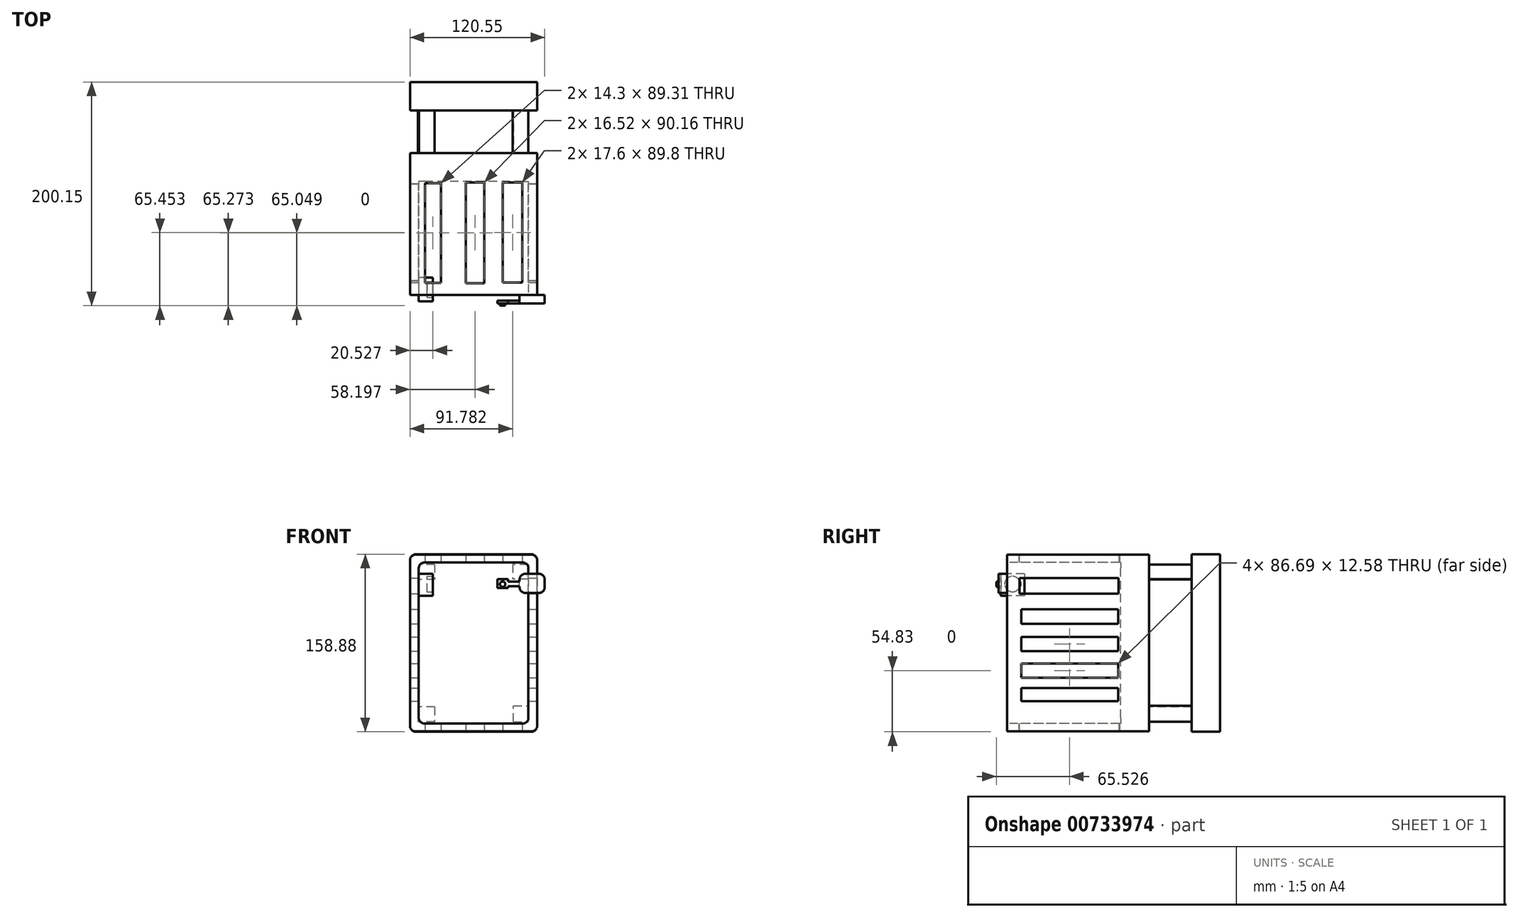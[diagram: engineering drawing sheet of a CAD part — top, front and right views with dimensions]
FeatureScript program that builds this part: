
annotation { "Feature Type Name" : "Feature", "Feature Type Description" : "" }
export const myFeature = defineFeature(function(context is Context, id is Id, definition is map)
    precondition{}
    {
        {
            var Q0;
            Q0=qCreatedBy(makeId("Front.planeOp"),FACE);
            var sketch = newSketch(context, id + "F0", { "sketchPlane" : qUnion([Q0])});
            skLineSegment(sketch, "E0.bottom", {"start": v(56.94, -79.1) * mm, "end": v(-56.94, -79.1) * mm});
            skLineSegment(sketch, "E0.top", {"start": v(56.94, 79.1) * mm, "end": v(-56.94, 79.1) * mm});
            skLineSegment(sketch, "E0.left", {"start": v(56.94, -79.1) * mm, "end": v(56.94, 79.1) * mm});
            skLineSegment(sketch, "E0.right", {"start": v(-56.94, -79.1) * mm, "end": v(-56.94, 79.1) * mm});
            skPoint(sketch, "E0.middle", {"position": v(0, 0) * mm});
            skSolve(sketch);
        }
        {
            var Q0;
            Q0=makeQuery(id+"F0.imprint","IMPRINT",FACE,{"disambiguationData":[TD([[makeQuery(id+"F0.imprint","IMPRINT",EDGE,{"derivedFrom":sQuery(id+"F0.wireOp",EDGE,"E0.bottom")}),-1.0]])]});
            extrude(context, id + "F1", {"entities" : qUnion([Q0]), "depth" : 127 * mm, "offsetDistance" : 25.4 * mm});
        }
        {
            var Q0;
            Q0=makeQuery(id+"F1.opExtrude","CAP_FACE",FACE,{"disambiguationData":[OSD([sQuery(id+"F0.wireOp",EDGE,"E0.bottom"),sQuery(id+"F0.wireOp",EDGE,"E0.top"),sQuery(id+"F0.wireOp",EDGE,"E0.left"),sQuery(id+"F0.wireOp",EDGE,"E0.right")])],"isStart":false});
            var sketch = newSketch(context, id + "F2", { "sketchPlane" : qUnion([Q0])});
            skLineSegment(sketch, "E1.bottom", {"start": v(49.08, -72.01) * mm, "end": v(-49.08, -72.01) * mm});
            skLineSegment(sketch, "E1.top", {"start": v(49.08, 72.01) * mm, "end": v(-49.08, 72.01) * mm});
            skLineSegment(sketch, "E1.left", {"start": v(49.08, -72.01) * mm, "end": v(49.08, 72.01) * mm});
            skLineSegment(sketch, "E1.right", {"start": v(-49.08, -72.01) * mm, "end": v(-49.08, 72.01) * mm});
            skPoint(sketch, "E1.middle", {"position": v(0, 0) * mm});
            skSolve(sketch);
        }
        {
            var Q0;
            Q0=makeQuery(id+"F2.imprint","IMPRINT",FACE,{"disambiguationData":[TD([[makeQuery(id+"F2.imprint","IMPRINT",EDGE,{"derivedFrom":sQuery(id+"F2.wireOp",EDGE,"E1.bottom")}),-1.0]])]});
            extrude(context, id + "F3", {"entities" : qUnion([Q0]), "operationType" : NewBodyOperationType.REMOVE, "oppositeDirection" : true, "depth" : 101.6 * mm, "offsetDistance" : 25.4 * mm});
        }
        {
            var Q0;
            Q0=makeQuery(id+"F1.opExtrude","SWEPT_FACE",FACE,{"disambiguationData":[OSD([sQuery(id+"F0.wireOp",EDGE,"E0.bottom")])]});
            var sketch = newSketch(context, id + "F4", { "sketchPlane" : qUnion([Q0])});
            skLineSegment(sketch, "E2.bottom", {"start": v(-43.56, 116.26) * mm, "end": v(-29.26, 116.26) * mm});
            skLineSegment(sketch, "E2.top", {"start": v(-43.56, 26.95) * mm, "end": v(-29.26, 26.95) * mm});
            skLineSegment(sketch, "E2.left", {"start": v(-43.56, 116.26) * mm, "end": v(-43.56, 26.95) * mm});
            skLineSegment(sketch, "E2.right", {"start": v(-29.26, 116.26) * mm, "end": v(-29.26, 26.95) * mm});
            skSolve(sketch);
        }
        {
            var Q0;
            Q0 = qSketchRegion(id + "F4", true);
            extrude(context, id + "F5", {"entities" : qUnion([Q0]), "operationType" : NewBodyOperationType.REMOVE, "endBound" : BoundingType.THROUGH_ALL, "oppositeDirection" : true, "depth" : 25.4 * mm, "offsetDistance" : 25.4 * mm});
        }
        {
            var Q0;
            Q0=makeQuery(id+"F1.opExtrude","SWEPT_FACE",FACE,{"disambiguationData":[OSD([sQuery(id+"F0.wireOp",EDGE,"E0.bottom")])]});
            var sketch = newSketch(context, id + "F6", { "sketchPlane" : qUnion([Q0])});
            skLineSegment(sketch, "E3.bottom", {"start": v(-7, 116.46) * mm, "end": v(9.52, 116.46) * mm});
            skLineSegment(sketch, "E3.top", {"start": v(-7, 26.3) * mm, "end": v(9.52, 26.3) * mm});
            skLineSegment(sketch, "E3.left", {"start": v(-7, 116.46) * mm, "end": v(-7, 26.3) * mm});
            skLineSegment(sketch, "E3.right", {"start": v(9.52, 116.46) * mm, "end": v(9.52, 26.3) * mm});
            skSolve(sketch);
        }
        {
            var Q0;
            Q0 = qSketchRegion(id + "F6", true);
            extrude(context, id + "F7", {"entities" : qUnion([Q0]), "operationType" : NewBodyOperationType.REMOVE, "endBound" : BoundingType.THROUGH_ALL, "oppositeDirection" : true, "depth" : 25.4 * mm, "offsetDistance" : 25.4 * mm});
        }
        {
            var Q0;
            Q0=makeQuery(id+"F1.opExtrude","SWEPT_FACE",FACE,{"disambiguationData":[OSD([sQuery(id+"F0.wireOp",EDGE,"E0.bottom")])]});
            var sketch = newSketch(context, id + "F8", { "sketchPlane" : qUnion([Q0])});
            skLineSegment(sketch, "E4.bottom", {"start": v(26.04, 116.1) * mm, "end": v(43.64, 116.1) * mm});
            skLineSegment(sketch, "E4.top", {"start": v(26.04, 26.3) * mm, "end": v(43.64, 26.3) * mm});
            skLineSegment(sketch, "E4.left", {"start": v(26.04, 116.1) * mm, "end": v(26.04, 26.3) * mm});
            skLineSegment(sketch, "E4.right", {"start": v(43.64, 116.1) * mm, "end": v(43.64, 26.3) * mm});
            skSolve(sketch);
        }
        {
            var Q0;
            Q0 = qSketchRegion(id + "F8", true);
            extrude(context, id + "F9", {"entities" : qUnion([Q0]), "operationType" : NewBodyOperationType.REMOVE, "endBound" : BoundingType.THROUGH_ALL, "oppositeDirection" : true, "depth" : 25.4 * mm, "offsetDistance" : 25.4 * mm});
        }
        {
            var Q0;
            Q0=makeQuery(id+"F1.opExtrude","SWEPT_FACE",FACE,{"disambiguationData":[OSD([sQuery(id+"F0.wireOp",EDGE,"E0.left")])]});
            var sketch = newSketch(context, id + "F10", { "sketchPlane" : qUnion([Q0])});
            skLineSegment(sketch, "E5.bottom", {"start": v(-115.88, 58.3) * mm, "end": v(-27.27, 58.3) * mm});
            skLineSegment(sketch, "E5.top", {"start": v(-115.88, 44.33) * mm, "end": v(-27.27, 44.33) * mm});
            skLineSegment(sketch, "E5.left", {"start": v(-115.88, 58.3) * mm, "end": v(-115.88, 44.33) * mm});
            skLineSegment(sketch, "E5.right", {"start": v(-27.27, 58.3) * mm, "end": v(-27.27, 44.33) * mm});
            skSolve(sketch);
        }
        {
            var Q0;
            Q0=makeQuery(id+"F10.imprint","IMPRINT",FACE,{"disambiguationData":[TD([[makeQuery(id+"F10.imprint","IMPRINT",EDGE,{"derivedFrom":sQuery(id+"F10.wireOp",EDGE,"E5.bottom")}),-1.0]])]});
            extrude(context, id + "F11", {"entities" : qUnion([Q0]), "operationType" : NewBodyOperationType.REMOVE, "endBound" : BoundingType.THROUGH_ALL, "oppositeDirection" : true, "depth" : 25.4 * mm, "offsetDistance" : 25.4 * mm});
        }
        {
            var Q0;
            Q0=makeQuery(id+"F1.opExtrude","SWEPT_FACE",FACE,{"disambiguationData":[OSD([sQuery(id+"F0.wireOp",EDGE,"E0.left")])]});
            var sketch = newSketch(context, id + "F12", { "sketchPlane" : qUnion([Q0])});
            skLineSegment(sketch, "E6.bottom", {"start": v(-114.2, 30.06) * mm, "end": v(-27.78, 30.06) * mm});
            skLineSegment(sketch, "E6.top", {"start": v(-114.2, 17.2) * mm, "end": v(-27.78, 17.2) * mm});
            skLineSegment(sketch, "E6.left", {"start": v(-114.2, 30.06) * mm, "end": v(-114.2, 17.2) * mm});
            skLineSegment(sketch, "E6.right", {"start": v(-27.78, 30.06) * mm, "end": v(-27.78, 17.2) * mm});
            skPoint(sketch, "E7.oppositeSnap0", {"position": v(-27.78, 23.63) * mm});
            skLineSegment(sketch, "E7.bottom", {"start": v(-114.47, 5.45) * mm, "end": v(-27.78, 5.45) * mm});
            skLineSegment(sketch, "E7.top", {"start": v(-114.47, -7.13) * mm, "end": v(-27.78, -7.13) * mm});
            skLineSegment(sketch, "E7.left", {"start": v(-114.47, 5.45) * mm, "end": v(-114.47, -7.13) * mm});
            skLineSegment(sketch, "E7.right", {"start": v(-27.78, 5.45) * mm, "end": v(-27.78, -7.13) * mm});
            skLineSegment(sketch, "E8.bottom", {"start": v(-114.47, -18.32) * mm, "end": v(-27.78, -18.32) * mm});
            skLineSegment(sketch, "E8.top", {"start": v(-114.47, -30.9) * mm, "end": v(-27.78, -30.9) * mm});
            skLineSegment(sketch, "E8.left", {"start": v(-114.47, -18.32) * mm, "end": v(-114.47, -30.9) * mm});
            skLineSegment(sketch, "E8.right", {"start": v(-27.78, -18.32) * mm, "end": v(-27.78, -30.9) * mm});
            skLineSegment(sketch, "E9.bottom", {"start": v(-114.47, -40.13) * mm, "end": v(-27.78, -40.13) * mm});
            skLineSegment(sketch, "E9.top", {"start": v(-114.47, -52.16) * mm, "end": v(-27.78, -52.16) * mm});
            skLineSegment(sketch, "E9.left", {"start": v(-114.47, -40.13) * mm, "end": v(-114.47, -52.16) * mm});
            skLineSegment(sketch, "E9.right", {"start": v(-27.78, -40.13) * mm, "end": v(-27.78, -52.16) * mm});
            skSolve(sketch);
        }
        {
            var Q0;
            Q0 = qSketchRegion(id + "F12", true);
            extrude(context, id + "F13", {"entities" : qUnion([Q0]), "operationType" : NewBodyOperationType.REMOVE, "endBound" : BoundingType.THROUGH_ALL, "oppositeDirection" : true, "depth" : 25.4 * mm, "offsetDistance" : 25.4 * mm});
        }
        {
            var Q0;
            Q0=makeQuery(id+"F1.opExtrude","SWEPT_EDGE",EDGE,{"disambiguationData":[OSD([sQuery(id+"F0.wireOp",EDGE,"E0.bottom"),sQuery(id+"F0.wireOp",EDGE,"E0.left")])]});
            var Q1;
            Q1=makeQuery(id+"F1.opExtrude","SWEPT_EDGE",EDGE,{"disambiguationData":[OSD([sQuery(id+"F0.wireOp",EDGE,"E0.bottom"),sQuery(id+"F0.wireOp",EDGE,"E0.right")])]});
            var Q2;
            Q2=makeQuery(id+"F1.opExtrude","SWEPT_EDGE",EDGE,{"disambiguationData":[OSD([sQuery(id+"F0.wireOp",EDGE,"E0.top"),sQuery(id+"F0.wireOp",EDGE,"E0.left")])]});
            var Q3;
            Q3=makeQuery(id+"F1.opExtrude","SWEPT_EDGE",EDGE,{"disambiguationData":[OSD([sQuery(id+"F0.wireOp",EDGE,"E0.top"),sQuery(id+"F0.wireOp",EDGE,"E0.right")])]});
            var Q4;
            Q4=makeQuery(id+"F3.boolean.opBoolean","COPY",EDGE,{"derivedFrom":makeQuery(id+"F3.opExtrude","SWEPT_EDGE",EDGE,{"disambiguationData":[OSD([sQuery(id+"F2.wireOp",EDGE,"E1.top"),sQuery(id+"F2.wireOp",EDGE,"E1.left")])]})});
            var Q5;
            Q5=makeQuery(id+"F3.boolean.opBoolean","COPY",EDGE,{"derivedFrom":makeQuery(id+"F3.opExtrude","SWEPT_EDGE",EDGE,{"disambiguationData":[OSD([sQuery(id+"F2.wireOp",EDGE,"E1.bottom"),sQuery(id+"F2.wireOp",EDGE,"E1.left")])]})});
            var Q6;
            Q6=makeQuery(id+"F3.boolean.opBoolean","COPY",EDGE,{"derivedFrom":makeQuery(id+"F3.opExtrude","SWEPT_EDGE",EDGE,{"disambiguationData":[OSD([sQuery(id+"F2.wireOp",EDGE,"E1.bottom"),sQuery(id+"F2.wireOp",EDGE,"E1.right")])]})});
            var Q7;
            Q7=makeQuery(id+"F3.boolean.opBoolean","COPY",EDGE,{"derivedFrom":makeQuery(id+"F3.opExtrude","SWEPT_EDGE",EDGE,{"disambiguationData":[OSD([sQuery(id+"F2.wireOp",EDGE,"E1.top"),sQuery(id+"F2.wireOp",EDGE,"E1.right")])]})});
            fillet(context, id + "F14", {"entities" : qUnion([Q0, Q1, Q2, Q3, Q4, Q5, Q6, Q7]), "radius" : 5.08 * mm, "tangentPropagation" : true, "allowEdgeOverflow" : false});
        }
        {
            var Q0;
            Q0=makeQuery(id+"F1.opExtrude","CAP_FACE",FACE,{"disambiguationData":[OSD([sQuery(id+"F0.wireOp",EDGE,"E0.bottom"),sQuery(id+"F0.wireOp",EDGE,"E0.top"),sQuery(id+"F0.wireOp",EDGE,"E0.left"),sQuery(id+"F0.wireOp",EDGE,"E0.right")])],"isStart":true});
            var sketch = newSketch(context, id + "F15", { "sketchPlane" : qUnion([Q0])});
            skLineSegment(sketch, "E10.bottom", {"start": v(-48.8, 70.33) * mm, "end": v(-34.82, 70.33) * mm});
            skLineSegment(sketch, "E10.top", {"start": v(-48.8, 57.2) * mm, "end": v(-34.82, 57.2) * mm});
            skLineSegment(sketch, "E10.left", {"start": v(-48.8, 70.33) * mm, "end": v(-48.8, 57.2) * mm});
            skLineSegment(sketch, "E10.right", {"start": v(-34.82, 70.33) * mm, "end": v(-34.82, 57.2) * mm});
            skLineSegment(sketch, "E11.bottom", {"start": v(34.82, 70.33) * mm, "end": v(48.8, 70.33) * mm});
            skLineSegment(sketch, "E11.top", {"start": v(34.82, 56.91) * mm, "end": v(48.8, 56.91) * mm});
            skLineSegment(sketch, "E11.left", {"start": v(34.82, 70.33) * mm, "end": v(34.82, 56.91) * mm});
            skLineSegment(sketch, "E11.right", {"start": v(48.8, 70.33) * mm, "end": v(48.8, 56.91) * mm});
            skLineSegment(sketch, "E12.bottom", {"start": v(34.82, -57.2) * mm, "end": v(49.92, -57.2) * mm});
            skLineSegment(sketch, "E12.top", {"start": v(34.82, -70.33) * mm, "end": v(49.92, -70.33) * mm});
            skLineSegment(sketch, "E12.left", {"start": v(34.82, -57.2) * mm, "end": v(34.82, -70.33) * mm});
            skLineSegment(sketch, "E12.right", {"start": v(49.92, -57.2) * mm, "end": v(49.92, -70.33) * mm});
            skLineSegment(sketch, "E13.bottom", {"start": v(-35.66, -70.33) * mm, "end": v(-49.08, -70.33) * mm});
            skLineSegment(sketch, "E13.top", {"start": v(-35.66, -56.07) * mm, "end": v(-49.08, -56.07) * mm});
            skLineSegment(sketch, "E13.left", {"start": v(-35.66, -70.33) * mm, "end": v(-35.66, -56.07) * mm});
            skLineSegment(sketch, "E13.right", {"start": v(-49.08, -70.33) * mm, "end": v(-49.08, -56.07) * mm});
            skSolve(sketch);
        }
        {
            var Q0;
            Q0 = qSketchRegion(id + "F15", true);
            extrude(context, id + "F16", {"entities" : qUnion([Q0]), "operationType" : NewBodyOperationType.ADD, "depth" : 38.1 * mm, "offsetDistance" : 25.4 * mm});
        }
        {
            var Q0;
            Q0=makeQuery(id+"F16.opExtrude","CAP_FACE",FACE,{"disambiguationData":[OSD([sQuery(id+"F15.wireOp",EDGE,"E12.bottom"),sQuery(id+"F15.wireOp",EDGE,"E12.top"),sQuery(id+"F15.wireOp",EDGE,"E12.left"),sQuery(id+"F15.wireOp",EDGE,"E12.right")])],"isStart":false});
            var sketch = newSketch(context, id + "F17", { "sketchPlane" : qUnion([Q0])});
            skLineSegment(sketch, "E14.bottom", {"start": v(56.72, -79.44) * mm, "end": v(-56.72, -79.44) * mm});
            skLineSegment(sketch, "E14.top", {"start": v(56.72, 79.44) * mm, "end": v(-56.72, 79.44) * mm});
            skLineSegment(sketch, "E14.left", {"start": v(56.72, -79.44) * mm, "end": v(56.72, 79.44) * mm});
            skLineSegment(sketch, "E14.right", {"start": v(-56.72, -79.44) * mm, "end": v(-56.72, 79.44) * mm});
            skPoint(sketch, "E14.middle", {"position": v(0, 0) * mm});
            skSolve(sketch);
        }
        {
            var Q0;
            Q0 = qSketchRegion(id + "F17", true);
            extrude(context, id + "F18", {"entities" : qUnion([Q0]), "operationType" : NewBodyOperationType.ADD, "depth" : 25.4 * mm, "offsetDistance" : 25.4 * mm});
        }
        {
            var Q0;
            Q0=makeQuery(id+"F18.opExtrude","SWEPT_EDGE",EDGE,{"disambiguationData":[OSD([sQuery(id+"F17.wireOp",EDGE,"E14.bottom"),sQuery(id+"F17.wireOp",EDGE,"E14.left")])]});
            var Q1;
            Q1=makeQuery(id+"F18.opExtrude","SWEPT_EDGE",EDGE,{"disambiguationData":[OSD([sQuery(id+"F17.wireOp",EDGE,"E14.bottom"),sQuery(id+"F17.wireOp",EDGE,"E14.right")])]});
            var Q2;
            Q2=makeQuery(id+"F18.opExtrude","SWEPT_EDGE",EDGE,{"disambiguationData":[OSD([sQuery(id+"F17.wireOp",EDGE,"E14.top"),sQuery(id+"F17.wireOp",EDGE,"E14.right")])]});
            var Q3;
            Q3=makeQuery(id+"F18.opExtrude","SWEPT_EDGE",EDGE,{"disambiguationData":[OSD([sQuery(id+"F17.wireOp",EDGE,"E14.top"),sQuery(id+"F17.wireOp",EDGE,"E14.left")])]});
            fillet(context, id + "F19", {"entities" : qUnion([Q0, Q1, Q2, Q3]), "radius" : 5.08 * mm, "tangentPropagation" : true, "allowEdgeOverflow" : false});
        }
        {
            var Q0;
            Q0=makeQuery(id+"F1.opExtrude","CAP_FACE",FACE,{"disambiguationData":[OSD([sQuery(id+"F0.wireOp",EDGE,"E0.bottom"),sQuery(id+"F0.wireOp",EDGE,"E0.top"),sQuery(id+"F0.wireOp",EDGE,"E0.left"),sQuery(id+"F0.wireOp",EDGE,"E0.right")])],"isStart":false});
            var sketch = newSketch(context, id + "F20", { "sketchPlane" : qUnion([Q0])});
            skLineSegment(sketch, "E15.bottom", {"start": v(63.61, 44.8) * mm, "end": v(41.14, 44.8) * mm});
            skLineSegment(sketch, "E15.top", {"start": v(63.61, 61.93) * mm, "end": v(41.14, 61.93) * mm});
            skLineSegment(sketch, "E15.left", {"start": v(63.61, 44.8) * mm, "end": v(63.61, 61.93) * mm});
            skLineSegment(sketch, "E15.right", {"start": v(41.14, 44.8) * mm, "end": v(41.14, 61.93) * mm});
            skPoint(sketch, "E15.middle", {"position": v(52.38, 53.36) * mm});
            skSolve(sketch);
        }
        {
            var Q0;
            Q0 = qSketchRegion(id + "F20", true);
            extrude(context, id + "F21", {"entities" : qUnion([Q0]), "operationType" : NewBodyOperationType.ADD, "depth" : 7.62 * mm, "offsetDistance" : 25.4 * mm});
        }
        {
            var Q0;
            Q0=makeQuery(id+"F21.opExtrude","SWEPT_EDGE",EDGE,{"disambiguationData":[OSD([sQuery(id+"F20.wireOp",EDGE,"E15.top"),sQuery(id+"F20.wireOp",EDGE,"E15.left")])]});
            var Q1;
            Q1=makeQuery(id+"F21.opExtrude","SWEPT_EDGE",EDGE,{"disambiguationData":[OSD([sQuery(id+"F20.wireOp",EDGE,"E15.bottom"),sQuery(id+"F20.wireOp",EDGE,"E15.left")])]});
            var Q2;
            Q2=makeQuery(id+"F21.opExtrude","SWEPT_EDGE",EDGE,{"disambiguationData":[OSD([sQuery(id+"F20.wireOp",EDGE,"E15.top"),sQuery(id+"F20.wireOp",EDGE,"E15.right")])]});
            var Q3;
            Q3=makeQuery(id+"F21.opExtrude","SWEPT_EDGE",EDGE,{"disambiguationData":[OSD([sQuery(id+"F20.wireOp",EDGE,"E15.bottom"),sQuery(id+"F20.wireOp",EDGE,"E15.right")])]});
            fillet(context, id + "F22", {"entities" : qUnion([Q0, Q1, Q2, Q3]), "radius" : 5.08 * mm, "tangentPropagation" : true, "allowEdgeOverflow" : false});
        }
        {
            var Q0;
            Q0=makeQuery(id+"F21.opExtrude","CAP_FACE",FACE,{"disambiguationData":[OSD([sQuery(id+"F20.wireOp",EDGE,"E15.bottom"),sQuery(id+"F20.wireOp",EDGE,"E15.top"),sQuery(id+"F20.wireOp",EDGE,"E15.left"),sQuery(id+"F20.wireOp",EDGE,"E15.right")])],"isStart":false});
            var sketch = newSketch(context, id + "F23", { "sketchPlane" : qUnion([Q0])});
            skLineSegment(sketch, "E16.bottom", {"start": v(29.34, 54.94) * mm, "end": v(47.82, 54.94) * mm});
            skLineSegment(sketch, "E16.top", {"start": v(29.34, 51) * mm, "end": v(47.82, 51) * mm});
            skLineSegment(sketch, "E16.left", {"start": v(29.34, 54.94) * mm, "end": v(29.34, 51) * mm});
            skLineSegment(sketch, "E16.right", {"start": v(47.82, 54.94) * mm, "end": v(47.82, 51) * mm});
            skLineSegment(sketch, "E17.bottom", {"start": v(21.3, 49.28) * mm, "end": v(30.72, 49.28) * mm});
            skLineSegment(sketch, "E17.top", {"start": v(21.3, 57.07) * mm, "end": v(30.72, 57.07) * mm});
            skLineSegment(sketch, "E17.left", {"start": v(21.3, 49.28) * mm, "end": v(21.3, 57.07) * mm});
            skLineSegment(sketch, "E17.right", {"start": v(30.72, 49.28) * mm, "end": v(30.72, 57.07) * mm});
            skCircle(sketch, "E18", {"center": v(25.4, 52.57) * mm, "radius": 1.89 * mm});
            skSolve(sketch);
        }
        {
            var Q0;
            Q0=makeQuery(id+"F23.imprint","IMPRINT",FACE,{"disambiguationData":[TD([[makeQuery(id+"F23.imprint","IMPRINT",EDGE,{"derivedFrom":sQuery(id+"F23.wireOp",EDGE,"E18")}),1.0]])]});
            var Q1;
            {var subQ0=sQuery(id+"F23.wireOp",EDGE,"E16.left");Q1=makeQuery(id+"F23.imprint","IMPRINT",FACE,{"disambiguationData":[TD([[makeQuery(id+"F23.imprint","IMPRINT",EDGE,{"derivedFrom":subQ0}),-1.0]])]});}
            var Q2;
            {var subQ0=sQuery(id+"F23.wireOp",EDGE,"E16.left");Q2=makeQuery(id+"F23.imprint","IMPRINT",FACE,{"disambiguationData":[TD([[makeQuery(id+"F23.imprint","IMPRINT",EDGE,{"derivedFrom":subQ0}),1.0]])]});}
            var Q3;
            {var subQ0=sQuery(id+"F23.wireOp",EDGE,"E17.right");var subQ1=sQuery(id+"F23.wireOp",EDGE,"E16.bottom");var subQ2=makeQuery(id+"F23.imprint","INTERSECT",VERTEX,{"derivedFrom":[subQ1,subQ0]});Q3=makeQuery(id+"F23.imprint","IMPRINT",FACE,{"disambiguationData":[TD([[makeQuery(id+"F23.imprint","IMPRINT",EDGE,{"disambiguationData":[TD([[subQ2,-1.0]])],"derivedFrom":subQ1}),-1.0]])]});}
            extrude(context, id + "F24", {"entities" : qUnion([Q0, Q1, Q2, Q3]), "operationType" : NewBodyOperationType.ADD, "oppositeDirection" : true, "depth" : 2.54 * mm, "offsetDistance" : 25.4 * mm});
        }
        {
            var Q0;
            {var subQ0=sQuery(id+"F20.wireOp",EDGE,"E15.right");Q0=makeQuery(id+"F24.boolean.opBoolean","MERGE",FACE,{"derivedFrom":[makeQuery(id+"F21.opExtrude","CAP_FACE",FACE,{"disambiguationData":[OSD([sQuery(id+"F20.wireOp",EDGE,"E15.bottom"),sQuery(id+"F20.wireOp",EDGE,"E15.top"),sQuery(id+"F20.wireOp",EDGE,"E15.left"),subQ0])],"isStart":false}),makeQuery(id+"F24.opExtrude","CAP_FACE",FACE,{"disambiguationData":[OSD([subQ0,sQuery(id+"F23.wireOp",EDGE,"E16.bottom"),sQuery(id+"F23.wireOp",EDGE,"E16.top"),sQuery(id+"F23.wireOp",EDGE,"E17.bottom"),sQuery(id+"F23.wireOp",EDGE,"E17.top"),sQuery(id+"F23.wireOp",EDGE,"E17.left"),sQuery(id+"F23.wireOp",EDGE,"E17.right")])],"isStart":true})]});}
            var sketch = newSketch(context, id + "F25", { "sketchPlane" : qUnion([Q0])});
            skCircle(sketch, "E19", {"center": v(26, 52.71) * mm, "radius": 2.4 * mm});
            skPoint(sketch, "E19.centerSnap0", {"position": v(26, 57.07) * mm});
            skSolve(sketch);
        }
        {
            var Q0;
            Q0 = qSketchRegion(id + "F25", true);
            extrude(context, id + "F26", {"entities" : qUnion([Q0]), "operationType" : NewBodyOperationType.ADD, "depth" : 2.03 * mm, "offsetDistance" : 25.4 * mm});
        }
        {
            var Q0;
            Q0=makeQuery(id+"F3.boolean.opBoolean","COPY",FACE,{"derivedFrom":makeQuery(id+"F3.opExtrude","SWEPT_FACE",FACE,{"disambiguationData":[OSD([sQuery(id+"F2.wireOp",EDGE,"E1.right")])]})});
            var sketch = newSketch(context, id + "F27", { "sketchPlane" : qUnion([Q0])});
            skLineSegment(sketch, "E20.bottom", {"start": v(-111.52, 62.03) * mm, "end": v(-132.82, 62.03) * mm});
            skLineSegment(sketch, "E20.top", {"start": v(-111.52, 42.24) * mm, "end": v(-132.82, 42.24) * mm});
            skLineSegment(sketch, "E20.left", {"start": v(-111.52, 62.03) * mm, "end": v(-111.52, 42.24) * mm});
            skLineSegment(sketch, "E20.right", {"start": v(-132.82, 62.03) * mm, "end": v(-132.82, 42.24) * mm});
            skSolve(sketch);
        }
        {
            var Q0;
            Q0 = qSketchRegion(id + "F27", true);
            extrude(context, id + "F28", {"entities" : qUnion([Q0]), "operationType" : NewBodyOperationType.ADD, "depth" : 12.7 * mm, "offsetDistance" : 25.4 * mm});
        }
        {
            var Q0;
            Q0=makeQuery(id+"F28.opExtrude","CAP_FACE",FACE,{"disambiguationData":[OSD([sQuery(id+"F27.wireOp",EDGE,"E20.bottom"),sQuery(id+"F27.wireOp",EDGE,"E20.top"),sQuery(id+"F27.wireOp",EDGE,"E20.left"),sQuery(id+"F27.wireOp",EDGE,"E20.right")])],"isStart":false});
            var sketch = newSketch(context, id + "F29", { "sketchPlane" : qUnion([Q0])});
            skCircle(sketch, "E21", {"center": v(-122.17, 52.78) * mm, "radius": 6.96 * mm});
            skPoint(sketch, "E21.centerSnap0", {"position": v(-122.17, 62.03) * mm});
            skSolve(sketch);
        }
        {
            var Q0;
            Q0 = qSketchRegion(id + "F29", true);
            extrude(context, id + "F30", {"entities" : qUnion([Q0]), "operationType" : NewBodyOperationType.REMOVE, "oppositeDirection" : true, "depth" : 5.08 * mm, "offsetDistance" : 25.4 * mm});
        }
    });
